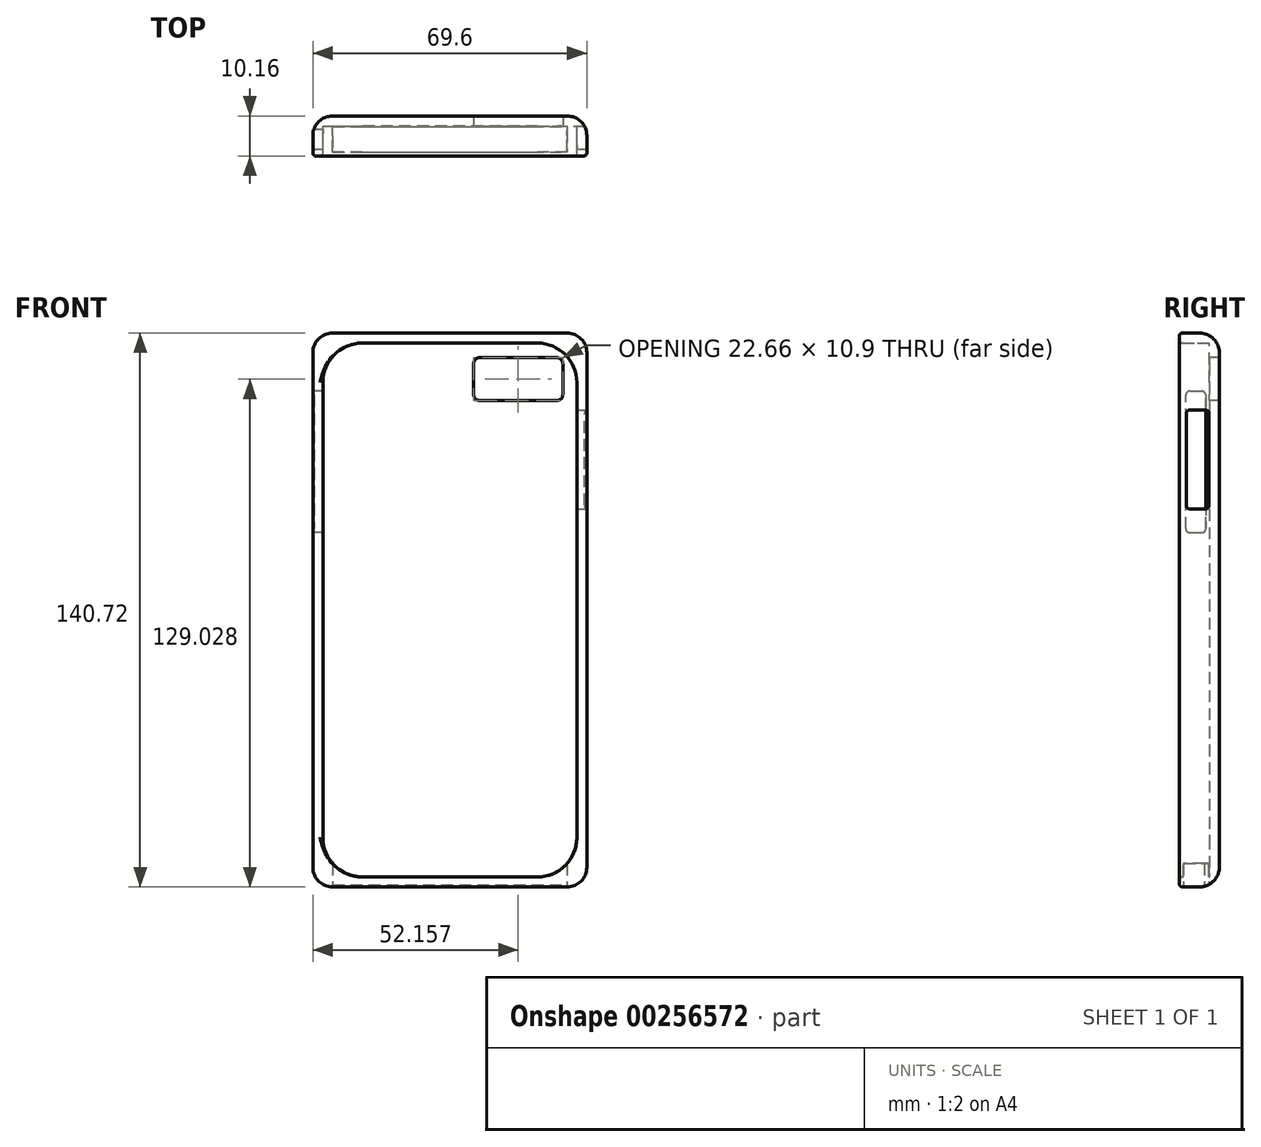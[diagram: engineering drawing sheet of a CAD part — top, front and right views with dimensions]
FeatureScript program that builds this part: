
annotation { "Feature Type Name" : "Feature", "Feature Type Description" : "" }
export const myFeature = defineFeature(function(context is Context, id is Id, definition is map)
    precondition{}
    {
        {
            var Q0;
            Q0=qCreatedBy(makeId("Front.planeOp"),FACE);
            var sketch = newSketch(context, id + "F0", { "sketchPlane" : qUnion([Q0])});
            skLineSegment(sketch, "E0.bottom", {"start": v(34.8, 70.36) * mm, "end": v(-34.8, 70.36) * mm});
            skLineSegment(sketch, "E0.top", {"start": v(34.8, -70.36) * mm, "end": v(-34.8, -70.36) * mm});
            skLineSegment(sketch, "E0.left", {"start": v(34.8, 70.36) * mm, "end": v(34.8, -70.36) * mm});
            skLineSegment(sketch, "E0.right", {"start": v(-34.8, 70.36) * mm, "end": v(-34.8, -70.36) * mm});
            skPoint(sketch, "E0.middle", {"position": v(0, 0) * mm});
            skSolve(sketch);
        }
        {
            var Q0;
            Q0=makeQuery(id+"F0.imprint","IMPRINT",FACE,{"disambiguationData":[TD([[makeQuery(id+"F0.imprint","IMPRINT",EDGE,{"derivedFrom":sQuery(id+"F0.wireOp",EDGE,"E0.bottom")}),1.0]])]});
            extrude(context, id + "F1", {"entities" : qUnion([Q0]), "endBound" : BoundingType.SYMMETRIC, "depth" : 10.16 * mm});
        }
        {
            var Q0;
            Q0=makeQuery(id+"F1.opExtrude","CAP_FACE",FACE,{"disambiguationData":[OSD([sQuery(id+"F0.wireOp",EDGE,"E0.bottom"),sQuery(id+"F0.wireOp",EDGE,"E0.top"),sQuery(id+"F0.wireOp",EDGE,"E0.left"),sQuery(id+"F0.wireOp",EDGE,"E0.right")])],"isStart":false});
            shell(context, id + "F2", {"entities" : qUnion([Q0]), "thickness" : 2.54 * mm});
        }
        {
            var Q0;
            Q0=makeQuery(id+"F1.opExtrude","SWEPT_EDGE",EDGE,{"disambiguationData":[OSD([sQuery(id+"F0.wireOp",EDGE,"E0.bottom"),sQuery(id+"F0.wireOp",EDGE,"E0.right")])]});
            var Q1;
            Q1=makeQuery(id+"F1.opExtrude","SWEPT_EDGE",EDGE,{"disambiguationData":[OSD([sQuery(id+"F0.wireOp",EDGE,"E0.bottom"),sQuery(id+"F0.wireOp",EDGE,"E0.left")])]});
            var Q2;
            Q2=makeQuery(id+"F1.opExtrude","SWEPT_EDGE",EDGE,{"disambiguationData":[OSD([sQuery(id+"F0.wireOp",EDGE,"E0.top"),sQuery(id+"F0.wireOp",EDGE,"E0.right")])]});
            var Q3;
            Q3=makeQuery(id+"F1.opExtrude","SWEPT_EDGE",EDGE,{"disambiguationData":[OSD([sQuery(id+"F0.wireOp",EDGE,"E0.top"),sQuery(id+"F0.wireOp",EDGE,"E0.left")])]});
            fillet(context, id + "F3", {"entities" : qUnion([Q0, Q1, Q2, Q3]), "radius" : 5 * mm, "tangentPropagation" : true, "allowEdgeOverflow" : false});
        }
        {
            var Q0;
            Q0=makeQuery(id+"F2.opShell","OFFSET_FACE",FACE,{"disambiguationData":[OSD([sQuery(id+"F0.wireOp",EDGE,"E0.bottom"),sQuery(id+"F0.wireOp",EDGE,"E0.top"),sQuery(id+"F0.wireOp",EDGE,"E0.left"),sQuery(id+"F0.wireOp",EDGE,"E0.right")])]});
            var sketch = newSketch(context, id + "F4", { "sketchPlane" : qUnion([Q0])});
            skLineSegment(sketch, "E1.bottom", {"start": v(6.02, 64.12) * mm, "end": v(28.69, 64.12) * mm});
            skLineSegment(sketch, "E1.top", {"start": v(6.02, 53.22) * mm, "end": v(28.69, 53.22) * mm});
            skLineSegment(sketch, "E1.left", {"start": v(6.02, 64.12) * mm, "end": v(6.02, 53.22) * mm});
            skLineSegment(sketch, "E1.right", {"start": v(28.69, 64.12) * mm, "end": v(28.69, 53.22) * mm});
            skSolve(sketch);
        }
        {
            var Q0;
            Q0=makeQuery(id+"F4.imprint","IMPRINT",FACE,{"disambiguationData":[TD([[makeQuery(id+"F4.imprint","IMPRINT",EDGE,{"derivedFrom":sQuery(id+"F4.wireOp",EDGE,"E1.bottom")}),-1.0]])]});
            extrude(context, id + "F5", {"entities" : qUnion([Q0]), "operationType" : NewBodyOperationType.REMOVE, "endBound" : BoundingType.SYMMETRIC, "oppositeDirection" : true, "depth" : 25 * mm});
        }
        {
            var Q0;
            Q0=makeQuery(id+"F1.opExtrude","SWEPT_FACE",FACE,{"disambiguationData":[OSD([sQuery(id+"F0.wireOp",EDGE,"E0.right")])]});
            var sketch = newSketch(context, id + "F6", { "sketchPlane" : qUnion([Q0])});
            skLineSegment(sketch, "E2.bottom", {"start": v(-1.63, 55.61) * mm, "end": v(3.41, 55.61) * mm});
            skLineSegment(sketch, "E2.top", {"start": v(-1.63, 19.64) * mm, "end": v(3.41, 19.64) * mm});
            skLineSegment(sketch, "E2.left", {"start": v(-1.63, 55.61) * mm, "end": v(-1.63, 19.64) * mm});
            skLineSegment(sketch, "E2.right", {"start": v(3.41, 55.61) * mm, "end": v(3.41, 19.64) * mm});
            skSolve(sketch);
        }
        {
            var Q0;
            Q0=makeQuery(id+"F6.imprint","IMPRINT",FACE,{"disambiguationData":[TD([[makeQuery(id+"F6.imprint","IMPRINT",EDGE,{"derivedFrom":sQuery(id+"F6.wireOp",EDGE,"E2.bottom")}),-1.0]])]});
            extrude(context, id + "F7", {"entities" : qUnion([Q0]), "operationType" : NewBodyOperationType.REMOVE, "endBound" : BoundingType.SYMMETRIC, "oppositeDirection" : true, "depth" : 25 * mm});
        }
        {
            var Q0;
            Q0=makeQuery(id+"F1.opExtrude","SWEPT_FACE",FACE,{"disambiguationData":[OSD([sQuery(id+"F0.wireOp",EDGE,"E0.left")])]});
            var sketch = newSketch(context, id + "F8", { "sketchPlane" : qUnion([Q0])});
            skLineSegment(sketch, "E3.bottom", {"start": v(-3.29, 50.87) * mm, "end": v(2.48, 50.87) * mm});
            skLineSegment(sketch, "E3.top", {"start": v(-3.29, 25.6) * mm, "end": v(2.48, 25.6) * mm});
            skLineSegment(sketch, "E3.left", {"start": v(-3.29, 50.87) * mm, "end": v(-3.29, 25.6) * mm});
            skLineSegment(sketch, "E3.right", {"start": v(2.48, 50.87) * mm, "end": v(2.48, 25.6) * mm});
            skSolve(sketch);
        }
        {
            var Q0;
            Q0=makeQuery(id+"F8.imprint","IMPRINT",FACE,{"disambiguationData":[TD([[makeQuery(id+"F8.imprint","IMPRINT",EDGE,{"derivedFrom":sQuery(id+"F8.wireOp",EDGE,"E3.bottom")}),-1.0]])]});
            extrude(context, id + "F9", {"entities" : qUnion([Q0]), "operationType" : NewBodyOperationType.REMOVE, "endBound" : BoundingType.SYMMETRIC, "oppositeDirection" : true, "depth" : 25 * mm});
        }
        {
            var Q0;
            Q0=makeQuery(id+"F1.opExtrude","CAP_EDGE",EDGE,{"disambiguationData":[OSD([sQuery(id+"F0.wireOp",EDGE,"E0.left")])],"isStart":true});
            fillet(context, id + "F10", {"entities" : qUnion([Q0]), "radius" : 5 * mm, "tangentPropagation" : true, "allowEdgeOverflow" : false});
        }
        {
            var Q0;
            Q0=makeQuery(id+"F1.opExtrude","SWEPT_FACE",FACE,{"disambiguationData":[OSD([sQuery(id+"F0.wireOp",EDGE,"E0.top")])]});
            var sketch = newSketch(context, id + "F11", { "sketchPlane" : qUnion([Q0])});
            skLineSegment(sketch, "E4.bottom", {"start": v(-29.8, 4.04) * mm, "end": v(29.8, 4.04) * mm});
            skLineSegment(sketch, "E4.top", {"start": v(-29.8, -1.34) * mm, "end": v(29.8, -1.34) * mm});
            skLineSegment(sketch, "E4.left", {"start": v(-29.8, 4.04) * mm, "end": v(-29.8, -1.34) * mm});
            skLineSegment(sketch, "E4.right", {"start": v(29.8, 4.04) * mm, "end": v(29.8, -1.34) * mm});
            skLineSegment(sketch, "E5.top", {"start": v(-29.8, -2.36) * mm, "end": v(29.8, -2.36) * mm});
            skLineSegment(sketch, "E5.left", {"start": v(-29.8, -1.34) * mm, "end": v(-29.8, -2.36) * mm});
            skLineSegment(sketch, "E5.right", {"start": v(29.8, -1.34) * mm, "end": v(29.8, -2.36) * mm});
            skSolve(sketch);
        }
        {
            var Q0;
            {var subQ0=sQuery(id+"F11.wireOp",EDGE,"E4.bottom");Q0=makeQuery(id+"F11.imprint","IMPRINT",FACE,{"disambiguationData":[TD([[makeQuery(id+"F11.imprint","IMPRINT",EDGE,{"derivedFrom":subQ0}),-1.0]])]});}
            var Q1;
            {var subQ0=sQuery(id+"F11.wireOp",EDGE,"E4.top");Q1=makeQuery(id+"F11.imprint","IMPRINT",FACE,{"disambiguationData":[TD([[makeQuery(id+"F11.imprint","IMPRINT",EDGE,{"derivedFrom":subQ0}),1.0]])]});}
            var Q2;
            {var subQ1=sQuery(id+"F0.wireOp",EDGE,"E0.top");var subQ2=makeQuery(id+"F10.opFillet","BLEND_EDGE",EDGE,{"blendedFrom":[makeQuery(id+"F1.opExtrude","CAP_EDGE",EDGE,{"disambiguationData":[OSD([subQ1])],"isStart":true}),makeQuery(id+"F1.opExtrude","SWEPT_FACE",FACE,{"disambiguationData":[OSD([subQ1])]})],"blendedInto":[makeQuery(id+"F1.opExtrude","SWEPT_FACE",FACE,{"disambiguationData":[OSD([subQ1])]})]});Q2=makeQuery(id+"F11.imprint","IMPRINT",FACE,{"disambiguationData":[TD([[makeQuery(id+"F11.imprint","IMPRINT",EDGE,{"derivedFrom":subQ2}),-1.0]])]});}
            var Q3;
            Q3=makeQuery(id+"F11.imprint","IMPRINT",FACE,{"disambiguationData":[TD([[makeQuery(id+"F11.imprint","IMPRINT",EDGE,{"derivedFrom":sQuery(id+"F11.wireOp",EDGE,"E5.top")}),1.0]])]});
            extrude(context, id + "F12", {"entities" : qUnion([Q0, Q1, Q2, Q3]), "operationType" : NewBodyOperationType.REMOVE, "endBound" : BoundingType.SYMMETRIC, "oppositeDirection" : true, "depth" : 25 * mm});
        }
        {
            var Q0;
            Q0=makeQuery(id+"F5.boolean.opBoolean","COPY",EDGE,{"derivedFrom":makeQuery(id+"F5.opExtrude","SWEPT_EDGE",EDGE,{"disambiguationData":[OSD([sQuery(id+"F4.wireOp",EDGE,"E1.top"),sQuery(id+"F4.wireOp",EDGE,"E1.left")])]})});
            var Q1;
            Q1=makeQuery(id+"F5.boolean.opBoolean","COPY",EDGE,{"derivedFrom":makeQuery(id+"F5.opExtrude","SWEPT_EDGE",EDGE,{"disambiguationData":[OSD([sQuery(id+"F4.wireOp",EDGE,"E1.top"),sQuery(id+"F4.wireOp",EDGE,"E1.right")])]})});
            var Q2;
            Q2=makeQuery(id+"F5.boolean.opBoolean","COPY",EDGE,{"derivedFrom":makeQuery(id+"F5.opExtrude","SWEPT_EDGE",EDGE,{"disambiguationData":[OSD([sQuery(id+"F4.wireOp",EDGE,"E1.bottom"),sQuery(id+"F4.wireOp",EDGE,"E1.right")])]})});
            var Q3;
            Q3=makeQuery(id+"F5.boolean.opBoolean","COPY",EDGE,{"derivedFrom":makeQuery(id+"F5.opExtrude","SWEPT_EDGE",EDGE,{"disambiguationData":[OSD([sQuery(id+"F4.wireOp",EDGE,"E1.bottom"),sQuery(id+"F4.wireOp",EDGE,"E1.left")])]})});
            fillet(context, id + "F13", {"entities" : qUnion([Q0, Q1, Q2, Q3]), "radius" : 1.52 * mm, "tangentPropagation" : true, "allowEdgeOverflow" : false});
        }
        {
            var Q0;
            Q0=makeQuery(id+"F7.boolean.opBoolean","COPY",EDGE,{"derivedFrom":makeQuery(id+"F7.opExtrude","SWEPT_EDGE",EDGE,{"disambiguationData":[OSD([sQuery(id+"F6.wireOp",EDGE,"E2.bottom"),sQuery(id+"F6.wireOp",EDGE,"E2.right")])]})});
            var Q1;
            Q1=makeQuery(id+"F7.boolean.opBoolean","COPY",EDGE,{"derivedFrom":makeQuery(id+"F7.opExtrude","SWEPT_EDGE",EDGE,{"disambiguationData":[OSD([sQuery(id+"F6.wireOp",EDGE,"E2.bottom"),sQuery(id+"F6.wireOp",EDGE,"E2.left")])]})});
            var Q2;
            Q2=makeQuery(id+"F7.boolean.opBoolean","COPY",EDGE,{"derivedFrom":makeQuery(id+"F7.opExtrude","SWEPT_EDGE",EDGE,{"disambiguationData":[OSD([sQuery(id+"F6.wireOp",EDGE,"E2.top"),sQuery(id+"F6.wireOp",EDGE,"E2.left")])]})});
            var Q3;
            Q3=makeQuery(id+"F7.boolean.opBoolean","COPY",EDGE,{"derivedFrom":makeQuery(id+"F7.opExtrude","SWEPT_EDGE",EDGE,{"disambiguationData":[OSD([sQuery(id+"F6.wireOp",EDGE,"E2.top"),sQuery(id+"F6.wireOp",EDGE,"E2.right")])]})});
            var Q4;
            Q4=makeQuery(id+"F9.boolean.opBoolean","COPY",EDGE,{"derivedFrom":makeQuery(id+"F9.opExtrude","SWEPT_EDGE",EDGE,{"disambiguationData":[OSD([sQuery(id+"F8.wireOp",EDGE,"E3.bottom"),sQuery(id+"F8.wireOp",EDGE,"E3.right")])]})});
            var Q5;
            Q5=makeQuery(id+"F9.boolean.opBoolean","COPY",EDGE,{"derivedFrom":makeQuery(id+"F9.opExtrude","SWEPT_EDGE",EDGE,{"disambiguationData":[OSD([sQuery(id+"F8.wireOp",EDGE,"E3.bottom"),sQuery(id+"F8.wireOp",EDGE,"E3.left")])]})});
            var Q6;
            Q6=makeQuery(id+"F9.boolean.opBoolean","COPY",EDGE,{"derivedFrom":makeQuery(id+"F9.opExtrude","SWEPT_EDGE",EDGE,{"disambiguationData":[OSD([sQuery(id+"F8.wireOp",EDGE,"E3.top"),sQuery(id+"F8.wireOp",EDGE,"E3.left")])]})});
            var Q7;
            Q7=makeQuery(id+"F9.boolean.opBoolean","COPY",EDGE,{"derivedFrom":makeQuery(id+"F9.opExtrude","SWEPT_EDGE",EDGE,{"disambiguationData":[OSD([sQuery(id+"F8.wireOp",EDGE,"E3.top"),sQuery(id+"F8.wireOp",EDGE,"E3.right")])]})});
            fillet(context, id + "F14", {"entities" : qUnion([Q0, Q1, Q2, Q3, Q4, Q5, Q6, Q7]), "radius" : 1.02 * mm, "tangentPropagation" : true, "allowEdgeOverflow" : false});
        }
        {
            var Q0;
            Q0=makeQuery(id+"F1.opExtrude","CAP_EDGE",EDGE,{"disambiguationData":[OSD([sQuery(id+"F0.wireOp",EDGE,"E0.right")])],"isStart":false});
            var Q1;
            {var subQ0=sQuery(id+"F0.wireOp",EDGE,"E0.right");Q1=makeQuery(id+"F2.opShell","OFFSET_EDGE",EDGE,{"disambiguationData":[OSD([subQ0]),TDD([makeQuery(id+"F1.opExtrude","CAP_EDGE",EDGE,{"disambiguationData":[OSD([subQ0])],"isStart":false})])]});}
            fillet(context, id + "F15", {"entities" : qUnion([Q0, Q1]), "radius" : 0.76 * mm, "tangentPropagation" : true, "allowEdgeOverflow" : false});
        }
        {
            var Q0;
            Q0=makeQuery(id+"F2.opShell","OFFSET_EDGE",EDGE,{"disambiguationData":[OSD([sQuery(id+"F0.wireOp",EDGE,"E0.bottom"),sQuery(id+"F0.wireOp",EDGE,"E0.right")])]});
            var Q1;
            Q1=makeQuery(id+"F2.opShell","OFFSET_EDGE",EDGE,{"disambiguationData":[OSD([sQuery(id+"F0.wireOp",EDGE,"E0.bottom"),sQuery(id+"F0.wireOp",EDGE,"E0.left")])]});
            var Q2;
            Q2=makeQuery(id+"F2.opShell","OFFSET_EDGE",EDGE,{"disambiguationData":[OSD([sQuery(id+"F0.wireOp",EDGE,"E0.top"),sQuery(id+"F0.wireOp",EDGE,"E0.left")])]});
            var Q3;
            Q3=makeQuery(id+"F2.opShell","OFFSET_EDGE",EDGE,{"disambiguationData":[OSD([sQuery(id+"F0.wireOp",EDGE,"E0.top"),sQuery(id+"F0.wireOp",EDGE,"E0.right")])]});
            fillet(context, id + "F16", {"entities" : qUnion([Q0, Q1, Q2, Q3]), "radius" : 10 * mm, "tangentPropagation" : true, "allowEdgeOverflow" : false});
        }
    });
